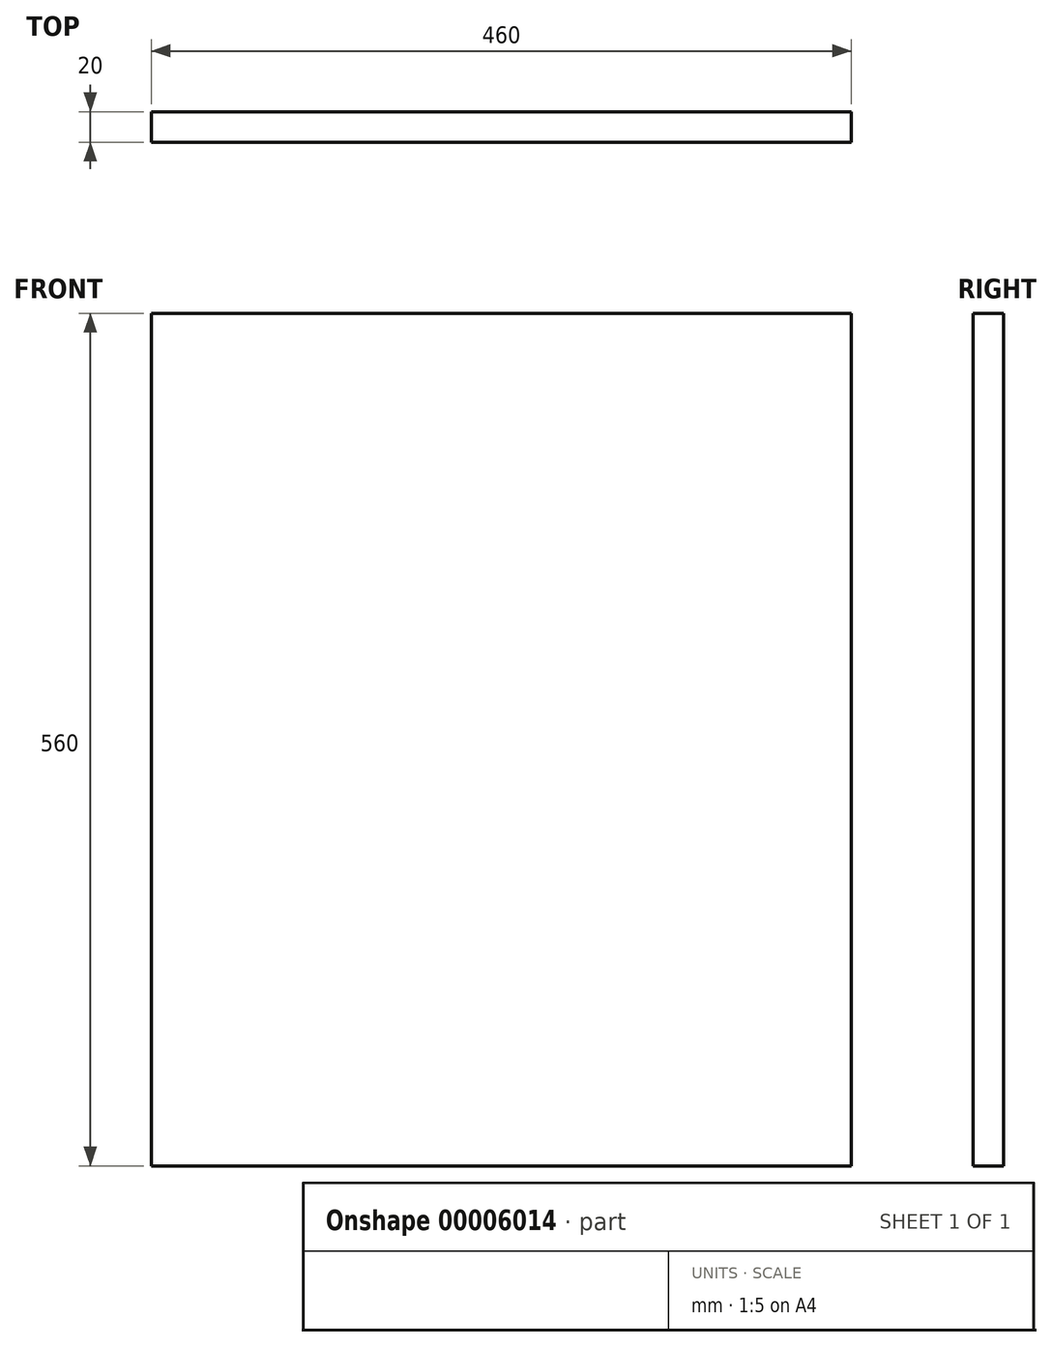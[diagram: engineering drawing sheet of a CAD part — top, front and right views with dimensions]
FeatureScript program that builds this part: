
annotation { "Feature Type Name" : "Feature", "Feature Type Description" : "" }
export const myFeature = defineFeature(function(context is Context, id is Id, definition is map)
    precondition{}
    {
        {
            var Q0;
            Q0=qCreatedBy(makeId("Front.planeOp"),FACE);
            var sketch = newSketch(context, id + "F0", { "sketchPlane" : qUnion([Q0])});
            skLineSegment(sketch, "E0.bottom", {"start": v(0, 0) * mm, "end": v(460, 0) * mm});
            skLineSegment(sketch, "E0.top", {"start": v(0, 560) * mm, "end": v(460, 560) * mm});
            skLineSegment(sketch, "E0.left", {"start": v(0, 0) * mm, "end": v(0, 560) * mm});
            skLineSegment(sketch, "E0.right", {"start": v(460, 0) * mm, "end": v(460, 560) * mm});
            skSolve(sketch);
        }
        {
            var Q0;
            Q0=makeQuery(id+"F0.imprint","IMPRINT",FACE,{"disambiguationData":[TD([[makeQuery(id+"F0.imprint","IMPRINT",EDGE,{"derivedFrom":sQuery(id+"F0.wireOp",EDGE,"E0.bottom")}),1.0]])]});
            extrude(context, id + "F1", {"entities" : qUnion([Q0]), "depth" : 20 * mm});
        }
    });
